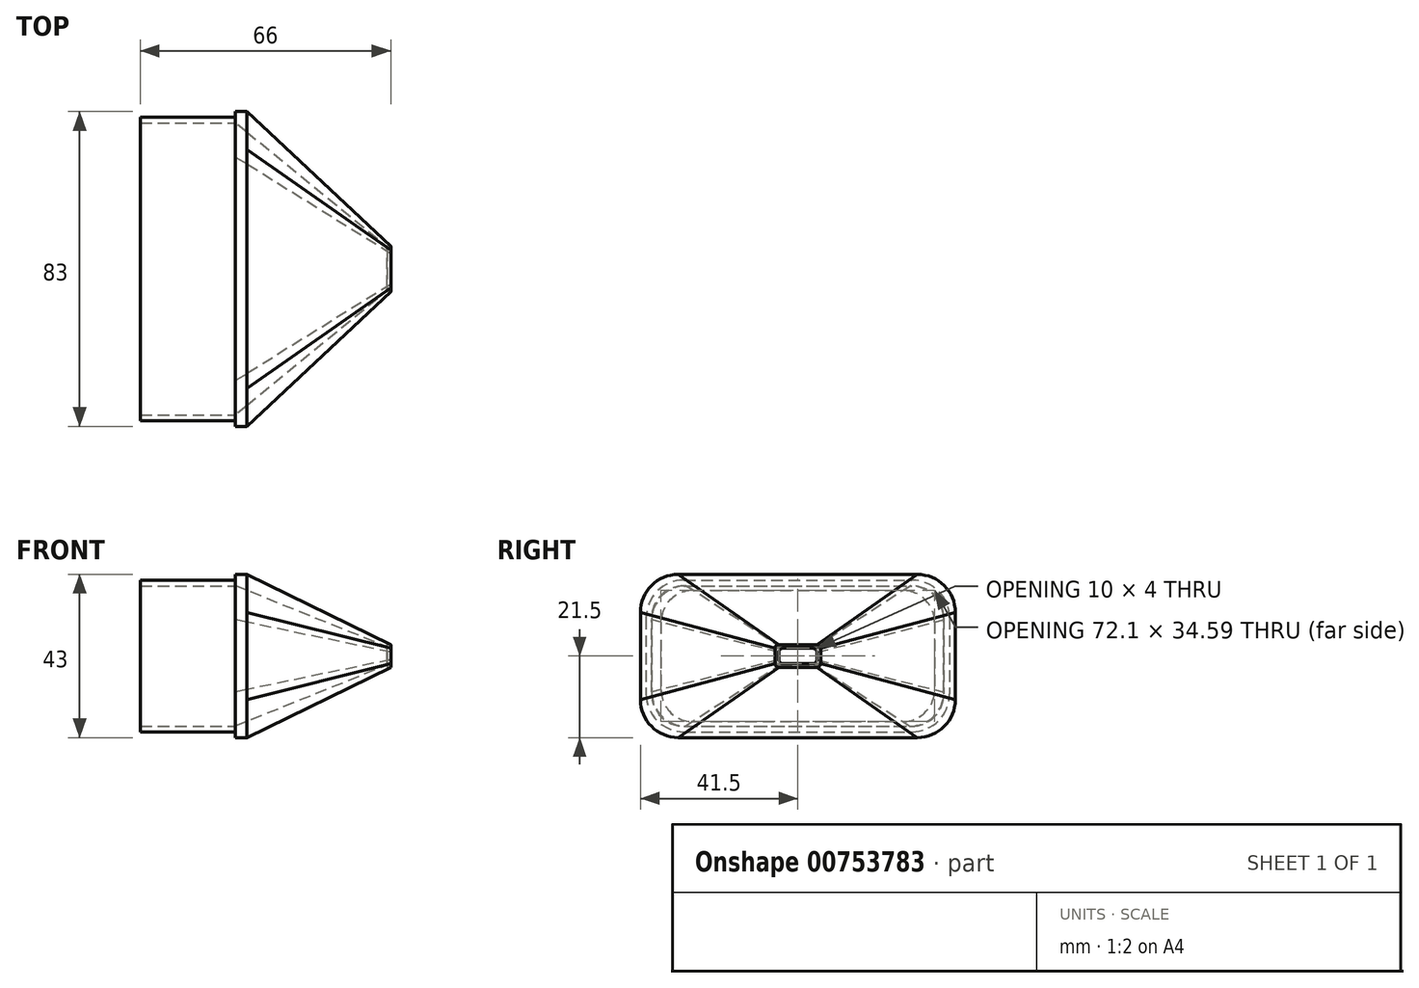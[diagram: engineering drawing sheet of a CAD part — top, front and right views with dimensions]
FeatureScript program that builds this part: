
annotation { "Feature Type Name" : "Feature", "Feature Type Description" : "" }
export const myFeature = defineFeature(function(context is Context, id is Id, definition is map)
    precondition{}
    {
        {
            var Q0;
            Q0=qCreatedBy(makeId("Right.planeOp"),FACE);
            var sketch = newSketch(context, id + "F0", { "sketchPlane" : qUnion([Q0])});
            skLineSegment(sketch, "E0.bottom", {"start": v(-30, 20) * mm, "end": v(30, 20) * mm});
            skLineSegment(sketch, "E0.top", {"start": v(-30, -20) * mm, "end": v(30, -20) * mm});
            skLineSegment(sketch, "E0.left", {"start": v(-40, 10) * mm, "end": v(-40, -10) * mm});
            skLineSegment(sketch, "E0.right", {"start": v(40, 10) * mm, "end": v(40, -10) * mm});
            skPoint(sketch, "E0.middle", {"position": v(0, 0) * mm});
            skPoint(sketch, "E1.visualSharp", {"position": v(-40, 20) * mm});
            skArc(sketch, "E1.filletArc", {"start": v(-30, 20) * mm, "mid": v(-37.07, 17.07) * mm, "end": v(-40, 10) * mm});
            skPoint(sketch, "E2.visualSharp", {"position": v(40, 20) * mm});
            skArc(sketch, "E2.filletArc", {"start": v(40, 10) * mm, "mid": v(37.07, 17.07) * mm, "end": v(30, 20) * mm});
            skPoint(sketch, "E3.visualSharp", {"position": v(40, -20) * mm});
            skArc(sketch, "E3.filletArc", {"start": v(30, -20) * mm, "mid": v(37.07, -17.07) * mm, "end": v(40, -10) * mm});
            skPoint(sketch, "E4.visualSharp", {"position": v(-40, -20) * mm});
            skArc(sketch, "E4.filletArc", {"start": v(-40, -10) * mm, "mid": v(-37.07, -17.07) * mm, "end": v(-30, -20) * mm});
            skLineSegment(sketch, "E5.0", {"start": v(38.5, 10) * mm, "end": v(38.5, -10) * mm});
            skArc(sketch, "E5.1", {"start": v(30, -18.5) * mm, "mid": v(36.01, -16.01) * mm, "end": v(38.5, -10) * mm});
            skArc(sketch, "E5.2", {"start": v(38.5, 10) * mm, "mid": v(36.01, 16.01) * mm, "end": v(30, 18.5) * mm});
            skLineSegment(sketch, "E5.3", {"start": v(-30, -18.5) * mm, "end": v(30, -18.5) * mm});
            skLineSegment(sketch, "E5.4", {"start": v(-30, 18.5) * mm, "end": v(30, 18.5) * mm});
            skArc(sketch, "E5.5", {"start": v(-30, 18.5) * mm, "mid": v(-36.01, 16.01) * mm, "end": v(-38.5, 10) * mm});
            skLineSegment(sketch, "E5.6", {"start": v(-38.5, 10) * mm, "end": v(-38.5, -10) * mm});
            skArc(sketch, "E5.7", {"start": v(-38.5, -10) * mm, "mid": v(-36.01, -16.01) * mm, "end": v(-30, -18.5) * mm});
            skSolve(sketch);
        }
        {
            var Q0;
            Q0=makeQuery(id+"F0.imprint","IMPRINT",FACE,{"disambiguationData":[TD([[makeQuery(id+"F0.imprint","IMPRINT",EDGE,{"derivedFrom":sQuery(id+"F0.wireOp",EDGE,"E0.bottom")}),-1.0]])]});
            extrude(context, id + "F1", {"entities" : qUnion([Q0]), "oppositeDirection" : true, "depth" : 25 * mm, "offsetDistance" : 25 * mm});
        }
        {
            var Q0;
            Q0=qCreatedBy(makeId("Right.planeOp"),FACE);
            cPlane(context, id + "F2", {"entities" : qUnion([Q0]), "cplaneType" : CPlaneType.OFFSET, "offset" : 40 * mm, "width" : 150 * mm, "height" : 150 * mm});
        }
        {
            var Q0;
            Q0=qCreatedBy(makeId("Right.planeOp"),FACE);
            var sketch = newSketch(context, id + "F3", { "sketchPlane" : qUnion([Q0])});
            skLineSegment(sketch, "E6.bottom", {"start": v(-31.5, -21.5) * mm, "end": v(31.5, -21.5) * mm});
            skLineSegment(sketch, "E6.top", {"start": v(-31.5, 21.5) * mm, "end": v(31.5, 21.5) * mm});
            skLineSegment(sketch, "E6.left", {"start": v(-41.5, -11.5) * mm, "end": v(-41.5, 11.5) * mm});
            skLineSegment(sketch, "E6.right", {"start": v(41.5, -11.5) * mm, "end": v(41.5, 11.5) * mm});
            skPoint(sketch, "E6.middle", {"position": v(0, 0) * mm});
            skPoint(sketch, "E7.visualSharp", {"position": v(-41.5, -21.5) * mm});
            skArc(sketch, "E7.filletArc", {"start": v(-41.5, -11.5) * mm, "mid": v(-38.57, -18.57) * mm, "end": v(-31.5, -21.5) * mm});
            skPoint(sketch, "E8.visualSharp", {"position": v(41.5, -21.5) * mm});
            skArc(sketch, "E8.filletArc", {"start": v(31.5, -21.5) * mm, "mid": v(38.57, -18.57) * mm, "end": v(41.5, -11.5) * mm});
            skPoint(sketch, "E9.visualSharp", {"position": v(41.5, 21.5) * mm});
            skArc(sketch, "E9.filletArc", {"start": v(41.5, 11.5) * mm, "mid": v(38.57, 18.57) * mm, "end": v(31.5, 21.5) * mm});
            skPoint(sketch, "E10.visualSharp", {"position": v(-41.5, 21.5) * mm});
            skArc(sketch, "E10.filletArc", {"start": v(-31.5, 21.5) * mm, "mid": v(-38.57, 18.57) * mm, "end": v(-41.5, 11.5) * mm});
            skSolve(sketch);
        }
        {
            var Q0;
            Q0=makeQuery(id+"F3.imprint","IMPRINT",FACE,{"disambiguationData":[TD([[makeQuery(id+"F3.imprint","IMPRINT",EDGE,{"derivedFrom":sQuery(id+"F3.wireOp",EDGE,"E6.bottom")}),1.0]])]});
            extrude(context, id + "F4", {"entities" : qUnion([Q0]), "operationType" : NewBodyOperationType.ADD, "depth" : 3 * mm, "offsetDistance" : 25 * mm});
        }
        {
            var Q0;
            Q0=qCreatedBy(id+"F2.planeOp",FACE);
            var sketch = newSketch(context, id + "F5", { "sketchPlane" : qUnion([Q0])});
            skLineSegment(sketch, "E11.bottom", {"start": v(5, -3) * mm, "end": v(-5, -3) * mm});
            skLineSegment(sketch, "E11.top", {"start": v(5, 3) * mm, "end": v(-5, 3) * mm});
            skLineSegment(sketch, "E11.left", {"start": v(6, -2) * mm, "end": v(6, 2) * mm});
            skLineSegment(sketch, "E11.right", {"start": v(-6, -2) * mm, "end": v(-6, 2) * mm});
            skPoint(sketch, "E12.visualSharp", {"position": v(4.5, -1.5) * mm});
            skPoint(sketch, "E13.visualSharp", {"position": v(4.5, 1.5) * mm});
            skPoint(sketch, "E14.visualSharp", {"position": v(6, -3) * mm});
            skArc(sketch, "E14.filletArc", {"start": v(5, -3) * mm, "mid": v(5.7, -2.7) * mm, "end": v(6, -2) * mm});
            skPoint(sketch, "E15.visualSharp", {"position": v(6, 3) * mm});
            skArc(sketch, "E15.filletArc", {"start": v(6, 2) * mm, "mid": v(5.7, 2.7) * mm, "end": v(5, 3) * mm});
            skPoint(sketch, "E16.visualSharp", {"position": v(-6, 3) * mm});
            skArc(sketch, "E16.filletArc", {"start": v(-5, 3) * mm, "mid": v(-5.7, 2.7) * mm, "end": v(-6, 2) * mm});
            skPoint(sketch, "E17.visualSharp", {"position": v(-6, -3) * mm});
            skArc(sketch, "E17.filletArc", {"start": v(-6, -2) * mm, "mid": v(-5.7, -2.7) * mm, "end": v(-5, -3) * mm});
            skSolve(sketch);
        }
        {
            var Q0;
            Q0=makeQuery(id+"F5.imprint","IMPRINT",FACE,{"disambiguationData":[TD([[makeQuery(id+"F5.imprint","IMPRINT",EDGE,{"derivedFrom":sQuery(id+"F5.wireOp",EDGE,"E11.bottom")}),-1.0]])]});
            extrude(context, id + "F6", {"entities" : qUnion([Q0]), "depth" : 1 * mm, "offsetDistance" : 25 * mm});
        }
        {
            var Q0;
            Q0=makeQuery(id+"F4.opExtrude","CAP_FACE",FACE,{"disambiguationData":[OSD([sQuery(id+"F3.wireOp",EDGE,"E6.bottom"),sQuery(id+"F3.wireOp",EDGE,"E6.top"),sQuery(id+"F3.wireOp",EDGE,"E6.left"),sQuery(id+"F3.wireOp",EDGE,"E6.right"),sQuery(id+"F3.wireOp",EDGE,"E7.filletArc"),sQuery(id+"F3.wireOp",EDGE,"E8.filletArc"),sQuery(id+"F3.wireOp",EDGE,"E9.filletArc"),sQuery(id+"F3.wireOp",EDGE,"E10.filletArc")])],"isStart":false});
            var Q1;
            Q1=makeQuery(id+"F6.opExtrude","CAP_FACE",FACE,{"disambiguationData":[OSD([sQuery(id+"F5.wireOp",EDGE,"E11.bottom"),sQuery(id+"F5.wireOp",EDGE,"E11.top"),sQuery(id+"F5.wireOp",EDGE,"E11.left"),sQuery(id+"F5.wireOp",EDGE,"E11.right"),sQuery(id+"F5.wireOp",EDGE,"E14.filletArc"),sQuery(id+"F5.wireOp",EDGE,"E15.filletArc"),sQuery(id+"F5.wireOp",EDGE,"E16.filletArc"),sQuery(id+"F5.wireOp",EDGE,"E17.filletArc")])],"isStart":false});
            loft(context, id + "F7", {"sheetProfilesArray" : [{ "sheetProfileEntities" : qUnion([Q0]) }, { "sheetProfileEntities" : qUnion([Q1]) }]});
        }
        {
            var Q0;
            Q0=makeQuery(id+"F6.opExtrude","CAP_FACE",FACE,{"disambiguationData":[OSD([sQuery(id+"F5.wireOp",EDGE,"E11.bottom"),sQuery(id+"F5.wireOp",EDGE,"E11.top"),sQuery(id+"F5.wireOp",EDGE,"E11.left"),sQuery(id+"F5.wireOp",EDGE,"E11.right"),sQuery(id+"F5.wireOp",EDGE,"E14.filletArc"),sQuery(id+"F5.wireOp",EDGE,"E15.filletArc"),sQuery(id+"F5.wireOp",EDGE,"E16.filletArc"),sQuery(id+"F5.wireOp",EDGE,"E17.filletArc")])],"isStart":false});
            var sketch = newSketch(context, id + "F8", { "sketchPlane" : qUnion([Q0])});
            skLineSegment(sketch, "E18.bottom", {"start": v(4, -2) * mm, "end": v(-4, -2) * mm});
            skLineSegment(sketch, "E18.top", {"start": v(4, 2) * mm, "end": v(-4, 2) * mm});
            skLineSegment(sketch, "E18.left", {"start": v(5, -1) * mm, "end": v(5, 1) * mm});
            skLineSegment(sketch, "E18.right", {"start": v(-5, -1) * mm, "end": v(-5, 1) * mm});
            skPoint(sketch, "E18.middle", {"position": v(0, 0) * mm});
            skPoint(sketch, "E19.visualSharp", {"position": v(5, -2) * mm});
            skArc(sketch, "E19.filletArc", {"start": v(4, -2) * mm, "mid": v(4.7, -1.7) * mm, "end": v(5, -1) * mm});
            skPoint(sketch, "E20.visualSharp", {"position": v(5, 2) * mm});
            skArc(sketch, "E20.filletArc", {"start": v(5, 1) * mm, "mid": v(4.7, 1.7) * mm, "end": v(4, 2) * mm});
            skPoint(sketch, "E21.visualSharp", {"position": v(-5, 2) * mm});
            skArc(sketch, "E21.filletArc", {"start": v(-4, 2) * mm, "mid": v(-4.7, 1.7) * mm, "end": v(-5, 1) * mm});
            skPoint(sketch, "E22.visualSharp", {"position": v(-5, -2) * mm});
            skArc(sketch, "E22.filletArc", {"start": v(-5, -1) * mm, "mid": v(-4.7, -1.7) * mm, "end": v(-4, -2) * mm});
            skSolve(sketch);
        }
        {
            var Q0;
            Q0=qCreatedBy(makeId("Right.planeOp"),FACE);
            var sketch = newSketch(context, id + "F9", { "sketchPlane" : qUnion([Q0])});
            skLineSegment(sketch, "E23.bottom", {"start": v(-29.5, -18.5) * mm, "end": v(29.5, -18.5) * mm});
            skLineSegment(sketch, "E23.top", {"start": v(-29.5, 18.5) * mm, "end": v(29.5, 18.5) * mm});
            skLineSegment(sketch, "E23.left", {"start": v(-38.5, -9.5) * mm, "end": v(-38.5, 9.5) * mm});
            skLineSegment(sketch, "E23.right", {"start": v(38.5, -9.5) * mm, "end": v(38.5, 9.5) * mm});
            skPoint(sketch, "E23.middle", {"position": v(0, 0) * mm});
            skPoint(sketch, "E24.visualSharp", {"position": v(-38.5, -18.5) * mm});
            skArc(sketch, "E24.filletArc", {"start": v(-38.5, -9.5) * mm, "mid": v(-35.86, -15.86) * mm, "end": v(-29.5, -18.5) * mm});
            skPoint(sketch, "E25.visualSharp", {"position": v(38.5, -18.5) * mm});
            skArc(sketch, "E25.filletArc", {"start": v(29.5, -18.5) * mm, "mid": v(35.86, -15.86) * mm, "end": v(38.5, -9.5) * mm});
            skPoint(sketch, "E26.visualSharp", {"position": v(38.5, 18.5) * mm});
            skArc(sketch, "E26.filletArc", {"start": v(38.5, 9.5) * mm, "mid": v(35.86, 15.86) * mm, "end": v(29.5, 18.5) * mm});
            skPoint(sketch, "E27.visualSharp", {"position": v(-38.5, 18.5) * mm});
            skArc(sketch, "E27.filletArc", {"start": v(-29.5, 18.5) * mm, "mid": v(-35.86, 15.86) * mm, "end": v(-38.5, 9.5) * mm});
            skSolve(sketch);
        }
        {
            var Q0;
            Q0=makeQuery(id+"F8.imprint","IMPRINT",FACE,{"disambiguationData":[TD([[makeQuery(id+"F8.imprint","IMPRINT",EDGE,{"derivedFrom":sQuery(id+"F8.wireOp",EDGE,"E18.bottom")}),-1.0]])]});
            var Q1;
            Q1=makeQuery(id+"F9.imprint","IMPRINT",FACE,{"disambiguationData":[TD([[makeQuery(id+"F9.imprint","IMPRINT",EDGE,{"derivedFrom":sQuery(id+"F9.wireOp",EDGE,"E23.bottom")}),1.0]])]});
            loft(context, id + "F10", {"operationType" : NewBodyOperationType.REMOVE, "sheetProfilesArray" : [{ "sheetProfileEntities" : qUnion([Q0]) }, { "sheetProfileEntities" : qUnion([Q1]) }]});
        }
    });
